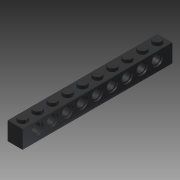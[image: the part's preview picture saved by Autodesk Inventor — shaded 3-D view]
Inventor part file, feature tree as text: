
AUTODESK INVENTOR PART (.ipt)
format: ipt  version: 2013 (Build 170138000, 138)  size: 200,192 bytes
history: native  units: mm
features: extrude x5, sketch x2, pattern_linear x2, plane x1, mirror x1
ambient origin geometry x8: Origin, YZ Plane, XZ Plane, XY Plane, X Axis, Y Axis, Z Axis, Center Point
bodies: Solid1 (feature_tree)
feature tree (11):
  sketch  "Sketch1"  dims[d0=8.0mm d1=8.0mm]
  extrude  "Extrusion1"  Depth=8.0mm
  extrude  "Extrusion2"  Depth=9.6mm TaperAngle=0.0deg
  extrude  "Extrusion3"  Depth=11.3mm TaperAngle=0.0deg
  pattern_linear  "Rectangular Pattern1"  Spacing1=1.7mm  [1 undecoded]
  sketch  "Sketch2"  dims[d2=4.8mm d3=9.6mm d4=0.0mm d5=11.3mm d6=0.0mm d7=1.7mm d8=0.0mm d9=100.0mm d11=8.0mm d12=4.8mm d14=6.2mm d15=1.7mm d16=0.0mm d17=0.8mm d18=0.0mm d19=90.0mm d21=8.0mm d22=8.0mm d23=5.6mm]
  plane  "Work Plane1"
  extrude  "Extrusion4"  Depth=100.0mm
  extrude  "Extrusion5"  Depth=4.8mm
  mirror  "Mirror1"
  pattern_linear  "Rectangular Pattern2"  Spacing1=6.2mm  [1 undecoded]
note: 2 required parameter values undecoded (feature->parameter linkage not recoverable at this tier; creation-order binding heuristic only, values carry confidence <= 0.55)
